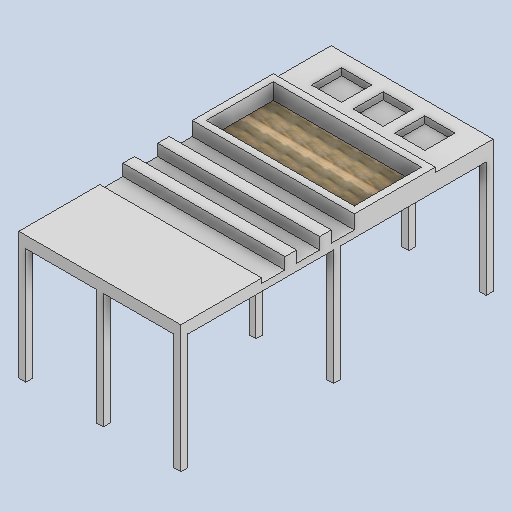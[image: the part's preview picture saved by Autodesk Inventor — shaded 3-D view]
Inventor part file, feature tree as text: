
AUTODESK INVENTOR PART (.ipt)
format: ipt  version: 2025 (Build 290162000, 162)  size: 400,896 bytes
history: native  units: in
note: dims shown in document units (in); Inventor stores cm internally (conversion verified against a paired STEP export)
features: extrude x8, sketch x4
ambient origin geometry x8: Origin, YZ Plane, XZ Plane, XY Plane, X Axis, Y Axis, Z Axis, Center Point
bodies: Solid1 (feature_tree)
feature tree (12):
  sketch  "Sketch1"  dims[d1=53.1496in d2=27.5591in]
  extrude  "Extrusion1"  Depth=27.5591in
  extrude  "Extrusion2"  Depth=15.748in
  extrude  "Extrusion3"  Depth=1.9685in TaperAngle=0.0deg
  extrude  "Extrusion4"  Depth=3.5433in TaperAngle=0.0deg
  sketch  "Sketch2"  dims[d3=13.7795in d4=15.748in]
  extrude  "Extrusion5"  Depth=2.7559in TaperAngle=0.0deg
  extrude  "Extrusion6"  Depth=1.1811in
  extrude  "Extrusion8"  Depth=1.1811in
  extrude  "Extrusion9"  Depth=1.1811in
  sketch  "Sketch4"  dims[d5=13.7795in d6=1.9685in d7=0.0in]
  sketch  "Sketch5"  dims[d8=1.1811in d9=0.0in d10=3.5433in d11=0.0in d12=2.7559in d13=0.0in d14=1.1811in d15=1.1811in d16=1.1811in d17=1.1811in d18=5.1181in d19=5.1181in d20=4.1339in d21=2.3622in d22=1.9685in d23=1.9685in d24=2.7559in d25=0.0in d26=1.9685in d27=0.0in d32=1.1811in d33=1.1811in d34=19.685in d35=0.0in d36=27.5591in d37=1.9685in d38=1.9685in d39=3.937in d40=3.937in d41=1.9685in d42=0.0in]
